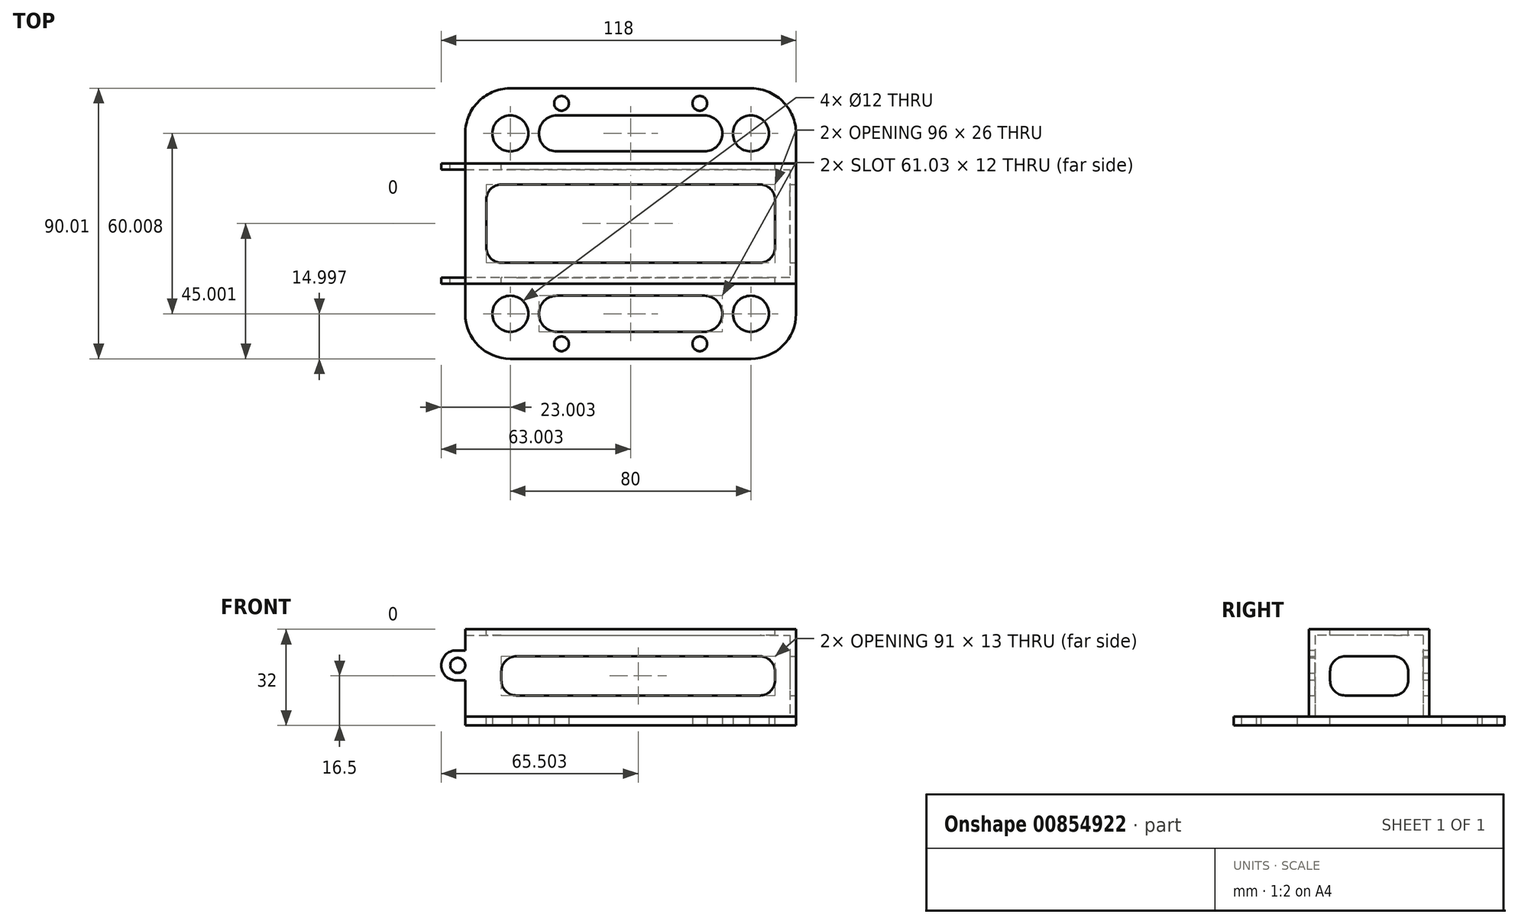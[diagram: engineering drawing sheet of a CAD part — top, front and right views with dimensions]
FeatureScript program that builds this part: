
annotation { "Feature Type Name" : "Feature", "Feature Type Description" : "" }
export const myFeature = defineFeature(function(context is Context, id is Id, definition is map)
    precondition{}
    {
        {
            var Q0;
            Q0=qCreatedBy(makeId("Top.planeOp"),FACE);
            var sketch = newSketch(context, id + "F0", { "sketchPlane" : qUnion([Q0])});
            skLineSegment(sketch, "E0.bottom", {"start": v(-43, 47.17) * mm, "end": v(36.02, 47.17) * mm});
            skLineSegment(sketch, "E0.top", {"start": v(-43.5, -42.83) * mm, "end": v(36.5, -42.83) * mm});
            skLineSegment(sketch, "E0.left", {"start": v(-58.5, 32.18) * mm, "end": v(-58.5, -27.83) * mm});
            skLineSegment(sketch, "E0.right", {"start": v(51.5, 32.18) * mm, "end": v(51.5, -27.83) * mm});
            skLineSegment(sketch, "E1.bottom", {"start": v(-26.5, 42.17) * mm, "end": v(19.5, 42.17) * mm, "construction": true});
            skLineSegment(sketch, "E1.top", {"start": v(-26.5, -37.83) * mm, "end": v(19.5, -37.83) * mm, "construction": true});
            skLineSegment(sketch, "E1.left", {"start": v(-26.5, 42.17) * mm, "end": v(-26.5, -37.83) * mm, "construction": true});
            skLineSegment(sketch, "E1.right", {"start": v(19.5, 42.17) * mm, "end": v(19.5, -37.83) * mm, "construction": true});
            skPoint(sketch, "E2", {"position": v(-3.5, 42.17) * mm});
            skLineSegment(sketch, "E3", {"start": v(-3.5, 42.17) * mm, "end": v(-3.5, 47.17) * mm, "construction": true});
            skPoint(sketch, "E4", {"position": v(-3.5, 47.17) * mm});
            skCircle(sketch, "E5", {"center": v(-26.5, 42.17) * mm, "radius": 2.45 * mm});
            skCircle(sketch, "E6", {"center": v(19.5, 42.17) * mm, "radius": 2.45 * mm});
            skCircle(sketch, "E7", {"center": v(19.5, -37.83) * mm, "radius": 2.45 * mm});
            skCircle(sketch, "E8", {"center": v(-26.5, -37.83) * mm, "radius": 2.45 * mm});
            skPoint(sketch, "E9", {"position": v(-58.5, 2.17) * mm});
            skLineSegment(sketch, "E10", {"start": v(-43.5, 2.17) * mm, "end": v(-58.5, 2.17) * mm, "construction": true});
            skPoint(sketch, "E11.visualSharp", {"position": v(-58.5, 47.17) * mm});
            skArc(sketch, "E11.filletArc", {"start": v(-43, 47.17) * mm, "mid": v(-53.93, 42.95) * mm, "end": v(-58.5, 32.18) * mm});
            skPoint(sketch, "E12.visualSharp", {"position": v(51.5, 47.17) * mm});
            skArc(sketch, "E12.filletArc", {"start": v(51.5, 32.18) * mm, "mid": v(46.94, 42.95) * mm, "end": v(36.02, 47.17) * mm});
            skPoint(sketch, "E13.visualSharp", {"position": v(51.5, -42.83) * mm});
            skArc(sketch, "E13.filletArc", {"start": v(36.5, -42.83) * mm, "mid": v(47.1, -38.44) * mm, "end": v(51.5, -27.83) * mm});
            skPoint(sketch, "E14.visualSharp", {"position": v(-58.5, -42.83) * mm});
            skArc(sketch, "E14.filletArc", {"start": v(-58.5, -27.83) * mm, "mid": v(-54.1, -38.44) * mm, "end": v(-43.5, -42.83) * mm});
            skCircle(sketch, "E15", {"center": v(-43.5, 32.18) * mm, "radius": 6 * mm});
            skCircle(sketch, "E16", {"center": v(36.5, 32.18) * mm, "radius": 6 * mm});
            skCircle(sketch, "E17", {"center": v(36.5, -27.83) * mm, "radius": 6 * mm});
            skCircle(sketch, "E18", {"center": v(-43.5, -27.83) * mm, "radius": 6 * mm});
            skLineSegment(sketch, "E19", {"start": v(-43.5, 32.18) * mm, "end": v(36.5, 32.18) * mm, "construction": true});
            skLineSegment(sketch, "E20", {"start": v(-43.5, -27.83) * mm, "end": v(36.5, -27.83) * mm, "construction": true});
            skLineSegment(sketch, "E21", {"start": v(21.02, 54.52) * mm, "end": v(21.02, -59.03) * mm, "construction": true});
            skLineSegment(sketch, "E22", {"start": v(-28, -54.44) * mm, "end": v(-28, 53.7) * mm, "construction": true});
            skArc(sketch, "E23", {"start": v(-28, 38.18) * mm, "mid": v(-34, 32.18) * mm, "end": v(-28, 26.18) * mm});
            skArc(sketch, "E24", {"start": v(21.02, 26.18) * mm, "mid": v(27.02, 32.18) * mm, "end": v(21.02, 38.18) * mm});
            skLineSegment(sketch, "E25", {"start": v(-28, 38.18) * mm, "end": v(21.02, 38.18) * mm});
            skLineSegment(sketch, "E26", {"start": v(-28, 26.18) * mm, "end": v(21.02, 26.18) * mm});
            skArc(sketch, "E27", {"start": v(-28, -21.83) * mm, "mid": v(-34, -27.83) * mm, "end": v(-28, -33.83) * mm});
            skArc(sketch, "E28", {"start": v(21.02, -33.83) * mm, "mid": v(27.02, -27.83) * mm, "end": v(21.02, -21.83) * mm});
            skLineSegment(sketch, "E29", {"start": v(-28, -21.83) * mm, "end": v(21.02, -21.83) * mm});
            skLineSegment(sketch, "E30", {"start": v(-28, -33.83) * mm, "end": v(21.02, -33.83) * mm});
            skSolve(sketch);
        }
        {
            var Q0;
            Q0 = qSketchRegion(id + "F0", true);
            extrude(context, id + "F1", {"entities" : qUnion([Q0]), "depth" : 3 * mm, "offsetDistance" : 25 * mm});
        }
        {
            var Q0;
            Q0=makeQuery(id+"F1.opExtrude","CAP_FACE",FACE,{"disambiguationData":[OSD([sQuery(id+"F0.wireOp",EDGE,"E0.bottom"),sQuery(id+"F0.wireOp",EDGE,"E0.top"),sQuery(id+"F0.wireOp",EDGE,"E0.left"),sQuery(id+"F0.wireOp",EDGE,"E0.right"),sQuery(id+"F0.wireOp",EDGE,"E5"),sQuery(id+"F0.wireOp",EDGE,"E6"),sQuery(id+"F0.wireOp",EDGE,"E7"),sQuery(id+"F0.wireOp",EDGE,"E8"),sQuery(id+"F0.wireOp",EDGE,"hCadaNJX-ca5q-XWxr-Yjam-UMz5wbafBlyw.bottom"),sQuery(id+"F0.wireOp",EDGE,"hCadaNJX-ca5q-XWxr-Yjam-UMz5wbafBlyw.top"),sQuery(id+"F0.wireOp",EDGE,"hCadaNJX-ca5q-XWxr-Yjam-UMz5wbafBlyw.left"),sQuery(id+"F0.wireOp",EDGE,"hCadaNJX-ca5q-XWxr-Yjam-UMz5wbafBlyw.right"),sQuery(id+"F0.wireOp",EDGE,"E11.filletArc"),sQuery(id+"F0.wireOp",EDGE,"E12.filletArc"),sQuery(id+"F0.wireOp",EDGE,"E13.filletArc"),sQuery(id+"F0.wireOp",EDGE,"E14.filletArc"),sQuery(id+"F0.wireOp",EDGE,"E15"),sQuery(id+"F0.wireOp",EDGE,"E16"),sQuery(id+"F0.wireOp",EDGE,"E17"),sQuery(id+"F0.wireOp",EDGE,"E18"),sQuery(id+"F0.wireOp",EDGE,"E23"),sQuery(id+"F0.wireOp",EDGE,"E24"),sQuery(id+"F0.wireOp",EDGE,"E25"),sQuery(id+"F0.wireOp",EDGE,"E26"),sQuery(id+"F0.wireOp",EDGE,"E27"),sQuery(id+"F0.wireOp",EDGE,"E28"),sQuery(id+"F0.wireOp",EDGE,"E29"),sQuery(id+"F0.wireOp",EDGE,"E30")])],"isStart":false});
            var sketch = newSketch(context, id + "F2", { "sketchPlane" : qUnion([Q0])});
            skLineSegment(sketch, "E31", {"start": v(-58.5, 2.17) * mm, "end": v(51.5, 2.17) * mm, "construction": true});
            skLineSegment(sketch, "E32", {"start": v(-3.5, 47.17) * mm, "end": v(-3.5, -42.83) * mm, "construction": true});
            skLineSegment(sketch, "E33", {"start": v(-58.5, 20.17) * mm, "end": v(49.5, 20.17) * mm});
            skLineSegment(sketch, "E34", {"start": v(51.5, 20.17) * mm, "end": v(51.5, -15.83) * mm});
            skLineSegment(sketch, "E35", {"start": v(49.5, -15.83) * mm, "end": v(-58.5, -15.83) * mm});
            skPoint(sketch, "E36", {"position": v(51.5, 2.17) * mm});
            skLineSegment(sketch, "E37", {"start": v(-58.5, 22.17) * mm, "end": v(51.5, 22.17) * mm});
            skLineSegment(sketch, "E38", {"start": v(-58.5, -17.83) * mm, "end": v(51.5, -17.83) * mm});
            skLineSegment(sketch, "E39", {"start": v(49.5, 20.17) * mm, "end": v(49.5, -15.83) * mm});
            skLineSegment(sketch, "E40", {"start": v(-58.5, -15.83) * mm, "end": v(-58.5, -17.83) * mm});
            skLineSegment(sketch, "E41", {"start": v(-58.5, 22.17) * mm, "end": v(-58.5, 20.17) * mm});
            skSolve(sketch);
        }
        {
            var Q0;
            Q0 = qSketchRegion(id + "F2", true);
            var Q1;
            Q1=makeQuery(id+"F2.imprint","IMPRINT",FACE,{"disambiguationData":[TD([[makeQuery(id+"F2.imprint","IMPRINT",EDGE,{"derivedFrom":sQuery(id+"F2.wireOp",EDGE,"E33")}),1.0]])]});
            extrude(context, id + "F3", {"entities" : qUnion([Q0, Q1]), "depth" : 27 * mm, "offsetDistance" : 25 * mm});
        }
        {
            var Q0;
            Q0=makeQuery(id+"F3.opExtrude","SWEPT_FACE",FACE,{"disambiguationData":[OSD([sQuery(id+"F0.wireOp",EDGE,"E0.right"),sQuery(id+"F2.wireOp",EDGE,"E34")])]});
            var sketch = newSketch(context, id + "F4", { "sketchPlane" : qUnion([Q0])});
            skLineSegment(sketch, "E42.bottom", {"start": v(-5.83, 23) * mm, "end": v(10.17, 23) * mm});
            skLineSegment(sketch, "E42.top", {"start": v(-5.83, 10) * mm, "end": v(10.17, 10) * mm});
            skLineSegment(sketch, "E42.left", {"start": v(-10.83, 18) * mm, "end": v(-10.83, 15) * mm});
            skLineSegment(sketch, "E42.right", {"start": v(15.17, 18) * mm, "end": v(15.17, 15) * mm});
            skPoint(sketch, "E43.visualSharp", {"position": v(-10.83, 23) * mm});
            skArc(sketch, "E43.filletArc", {"start": v(-5.83, 23) * mm, "mid": v(-9.36, 21.54) * mm, "end": v(-10.83, 18) * mm});
            skPoint(sketch, "E44.visualSharp", {"position": v(-10.83, 10) * mm});
            skArc(sketch, "E44.filletArc", {"start": v(-10.83, 15) * mm, "mid": v(-9.36, 11.46) * mm, "end": v(-5.83, 10) * mm});
            skPoint(sketch, "E45.visualSharp", {"position": v(15.17, 10) * mm});
            skArc(sketch, "E45.filletArc", {"start": v(10.17, 10) * mm, "mid": v(13.7, 11.46) * mm, "end": v(15.17, 15) * mm});
            skPoint(sketch, "E46.visualSharp", {"position": v(15.17, 23) * mm});
            skArc(sketch, "E46.filletArc", {"start": v(15.17, 18) * mm, "mid": v(13.7, 21.54) * mm, "end": v(10.17, 23) * mm});
            skSolve(sketch);
        }
        {
            var Q0;
            Q0 = qSketchRegion(id + "F4", true);
            extrude(context, id + "F5", {"entities" : qUnion([Q0]), "operationType" : NewBodyOperationType.REMOVE, "oppositeDirection" : true, "depth" : 25 * mm, "offsetDistance" : 25 * mm});
        }
        {
            var Q0;
            Q0=makeQuery(id+"F3.opExtrude","SWEPT_FACE",FACE,{"disambiguationData":[OSD([sQuery(id+"F2.wireOp",EDGE,"E37")])]});
            var sketch = newSketch(context, id + "F6", { "sketchPlane" : qUnion([Q0])});
            skLineSegment(sketch, "E47.bottom", {"start": v(-39.5, 23) * mm, "end": v(41.5, 23) * mm});
            skLineSegment(sketch, "E47.top", {"start": v(-39.5, 10) * mm, "end": v(41.5, 10) * mm});
            skLineSegment(sketch, "E47.left", {"start": v(-44.5, 18) * mm, "end": v(-44.5, 15) * mm});
            skLineSegment(sketch, "E47.right", {"start": v(46.5, 18) * mm, "end": v(46.5, 15) * mm});
            skPoint(sketch, "E48.visualSharp", {"position": v(-44.5, 23) * mm});
            skArc(sketch, "E48.filletArc", {"start": v(-39.5, 23) * mm, "mid": v(-43.04, 21.54) * mm, "end": v(-44.5, 18) * mm});
            skPoint(sketch, "E49.visualSharp", {"position": v(-44.5, 10) * mm});
            skArc(sketch, "E49.filletArc", {"start": v(-44.5, 15) * mm, "mid": v(-43.04, 11.46) * mm, "end": v(-39.5, 10) * mm});
            skPoint(sketch, "E50.visualSharp", {"position": v(46.5, 10) * mm});
            skArc(sketch, "E50.filletArc", {"start": v(41.5, 10) * mm, "mid": v(45.03, 11.46) * mm, "end": v(46.5, 15) * mm});
            skPoint(sketch, "E51.visualSharp", {"position": v(46.5, 23) * mm});
            skArc(sketch, "E51.filletArc", {"start": v(46.5, 18) * mm, "mid": v(45.03, 21.54) * mm, "end": v(41.5, 23) * mm});
            skSolve(sketch);
        }
        {
            var Q0;
            Q0 = qSketchRegion(id + "F6", true);
            extrude(context, id + "F7", {"entities" : qUnion([Q0]), "operationType" : NewBodyOperationType.REMOVE, "oppositeDirection" : true, "depth" : 100 * mm, "offsetDistance" : 25 * mm});
        }
        {
            var Q0;
            Q0=makeQuery(id+"F3.opExtrude","CAP_FACE",FACE,{"disambiguationData":[OSD([sQuery(id+"F0.wireOp",EDGE,"E0.right"),sQuery(id+"F2.wireOp",EDGE,"E33"),sQuery(id+"F2.wireOp",EDGE,"E34"),sQuery(id+"F2.wireOp",EDGE,"E35"),sQuery(id+"F2.wireOp",EDGE,"E37"),sQuery(id+"F2.wireOp",EDGE,"E38"),sQuery(id+"F2.wireOp",EDGE,"E39"),sQuery(id+"F2.wireOp",EDGE,"E40"),sQuery(id+"F2.wireOp",EDGE,"E41")])],"isStart":false});
            var sketch = newSketch(context, id + "F8", { "sketchPlane" : qUnion([Q0])});
            skLineSegment(sketch, "E52.bottom", {"start": v(-58.5, 22.17) * mm, "end": v(51.5, 22.17) * mm});
            skLineSegment(sketch, "E52.top", {"start": v(-58.5, -17.83) * mm, "end": v(51.5, -17.83) * mm});
            skLineSegment(sketch, "E52.left", {"start": v(-58.5, 22.17) * mm, "end": v(-58.5, -17.83) * mm});
            skLineSegment(sketch, "E52.right", {"start": v(51.5, 22.17) * mm, "end": v(51.5, -17.83) * mm});
            skSolve(sketch);
        }
        {
            var Q0;
            Q0 = qSketchRegion(id + "F8", true);
            extrude(context, id + "F9", {"entities" : qUnion([Q0]), "operationType" : NewBodyOperationType.ADD, "depth" : 2 * mm, "offsetDistance" : 25 * mm});
        }
        {
            var Q0;
            Q0=makeQuery(id+"F9.opExtrude","CAP_FACE",FACE,{"disambiguationData":[OSD([sQuery(id+"F8.wireOp",EDGE,"E52.bottom"),sQuery(id+"F8.wireOp",EDGE,"E52.top"),sQuery(id+"F8.wireOp",EDGE,"E52.left"),sQuery(id+"F8.wireOp",EDGE,"E52.right")])],"isStart":false});
            var sketch = newSketch(context, id + "F10", { "sketchPlane" : qUnion([Q0])});
            skLineSegment(sketch, "E53.bottom", {"start": v(-46.5, 15.17) * mm, "end": v(39.5, 15.17) * mm});
            skLineSegment(sketch, "E53.top", {"start": v(-46.5, -10.83) * mm, "end": v(39.5, -10.83) * mm});
            skLineSegment(sketch, "E53.left", {"start": v(-51.5, 10.17) * mm, "end": v(-51.5, -5.83) * mm});
            skLineSegment(sketch, "E53.right", {"start": v(44.5, 10.17) * mm, "end": v(44.5, -5.83) * mm});
            skPoint(sketch, "E54.visualSharp", {"position": v(-51.5, 15.17) * mm});
            skArc(sketch, "E54.filletArc", {"start": v(-46.5, 15.17) * mm, "mid": v(-50.03, 13.7) * mm, "end": v(-51.5, 10.17) * mm});
            skPoint(sketch, "E55.visualSharp", {"position": v(44.5, 15.17) * mm});
            skArc(sketch, "E55.filletArc", {"start": v(44.5, 10.17) * mm, "mid": v(43.04, 13.7) * mm, "end": v(39.5, 15.17) * mm});
            skPoint(sketch, "E56.visualSharp", {"position": v(44.5, -10.83) * mm});
            skArc(sketch, "E56.filletArc", {"start": v(39.5, -10.83) * mm, "mid": v(43.04, -9.36) * mm, "end": v(44.5, -5.83) * mm});
            skPoint(sketch, "E57.visualSharp", {"position": v(-51.5, -10.83) * mm});
            skArc(sketch, "E57.filletArc", {"start": v(-51.5, -5.83) * mm, "mid": v(-50.03, -9.36) * mm, "end": v(-46.5, -10.83) * mm});
            skSolve(sketch);
        }
        {
            var Q0;
            Q0 = qSketchRegion(id + "F10", true);
            extrude(context, id + "F11", {"entities" : qUnion([Q0]), "operationType" : NewBodyOperationType.REMOVE, "oppositeDirection" : true, "depth" : 50 * mm, "offsetDistance" : 25 * mm});
        }
        {
            var Q0;
            Q0=makeQuery(id+"F9.boolean.opBoolean","MERGE",FACE,{"derivedFrom":[makeQuery(id+"F3.opExtrude","SWEPT_FACE",FACE,{"disambiguationData":[OSD([sQuery(id+"F2.wireOp",EDGE,"E40")])]}),makeQuery(id+"F3.opExtrude","SWEPT_FACE",FACE,{"disambiguationData":[OSD([sQuery(id+"F2.wireOp",EDGE,"E41")])]}),makeQuery(id+"F9.opExtrude","SWEPT_FACE",FACE,{"disambiguationData":[OSD([sQuery(id+"F8.wireOp",EDGE,"E52.left")])]})]});
            var sketch = newSketch(context, id + "F12", { "sketchPlane" : qUnion([Q0])});
            skLineSegment(sketch, "E58.bottom", {"start": v(-22.17, 25) * mm, "end": v(-20.17, 25) * mm});
            skLineSegment(sketch, "E58.top", {"start": v(-22.17, 15) * mm, "end": v(-20.17, 15) * mm});
            skLineSegment(sketch, "E58.left", {"start": v(-22.17, 25) * mm, "end": v(-22.17, 15) * mm});
            skLineSegment(sketch, "E58.right", {"start": v(-20.17, 25) * mm, "end": v(-20.17, 15) * mm});
            skLineSegment(sketch, "E59.bottom", {"start": v(15.83, 25) * mm, "end": v(17.83, 25) * mm});
            skLineSegment(sketch, "E59.top", {"start": v(15.83, 15) * mm, "end": v(17.83, 15) * mm});
            skLineSegment(sketch, "E59.left", {"start": v(15.83, 25) * mm, "end": v(15.83, 15) * mm});
            skLineSegment(sketch, "E59.right", {"start": v(17.83, 25) * mm, "end": v(17.83, 15) * mm});
            skSolve(sketch);
        }
        {
            var Q0;
            Q0 = qSketchRegion(id + "F12", true);
            extrude(context, id + "F13", {"entities" : qUnion([Q0]), "operationType" : NewBodyOperationType.ADD, "depth" : 8 * mm, "offsetDistance" : 25 * mm});
        }
        {
            var Q0;
            Q0=makeQuery(id+"F13.boolean.opBoolean","MERGE",FACE,{"derivedFrom":[makeQuery(id+"F9.boolean.opBoolean","MERGE",FACE,{"derivedFrom":[makeQuery(id+"F3.opExtrude","SWEPT_FACE",FACE,{"disambiguationData":[OSD([sQuery(id+"F2.wireOp",EDGE,"E37")])]}),makeQuery(id+"F9.opExtrude","SWEPT_FACE",FACE,{"disambiguationData":[OSD([sQuery(id+"F8.wireOp",EDGE,"E52.bottom")])]})]}),makeQuery(id+"F13.opExtrude","SWEPT_FACE",FACE,{"disambiguationData":[OSD([sQuery(id+"F12.wireOp",EDGE,"E58.left")])]})]});
            var sketch = newSketch(context, id + "F14", { "sketchPlane" : qUnion([Q0])});
            skCircle(sketch, "E60", {"center": v(61, 20) * mm, "radius": 2.5 * mm});
            skSolve(sketch);
        }
        {
            var Q0;
            Q0 = qSketchRegion(id + "F14", true);
            extrude(context, id + "F15", {"entities" : qUnion([Q0]), "operationType" : NewBodyOperationType.REMOVE, "oppositeDirection" : true, "depth" : 50 * mm, "offsetDistance" : 25 * mm});
        }
        {
            var Q0;
            Q0=makeQuery(id+"F13.opExtrude","CAP_EDGE",EDGE,{"disambiguationData":[OSD([sQuery(id+"F12.wireOp",EDGE,"E59.bottom")])],"isStart":false});
            var Q1;
            Q1=makeQuery(id+"F13.opExtrude","CAP_EDGE",EDGE,{"disambiguationData":[OSD([sQuery(id+"F12.wireOp",EDGE,"E59.top")])],"isStart":false});
            var Q2;
            Q2=makeQuery(id+"F13.opExtrude","CAP_EDGE",EDGE,{"disambiguationData":[OSD([sQuery(id+"F12.wireOp",EDGE,"E58.top")])],"isStart":false});
            var Q3;
            Q3=makeQuery(id+"F13.opExtrude","CAP_EDGE",EDGE,{"disambiguationData":[OSD([sQuery(id+"F12.wireOp",EDGE,"E58.bottom")])],"isStart":false});
            fillet(context, id + "F16", {"entities" : qUnion([Q0, Q1, Q2, Q3]), "radius" : 5 * mm, "tangentPropagation" : true, "allowEdgeOverflow" : false});
        }
    });
